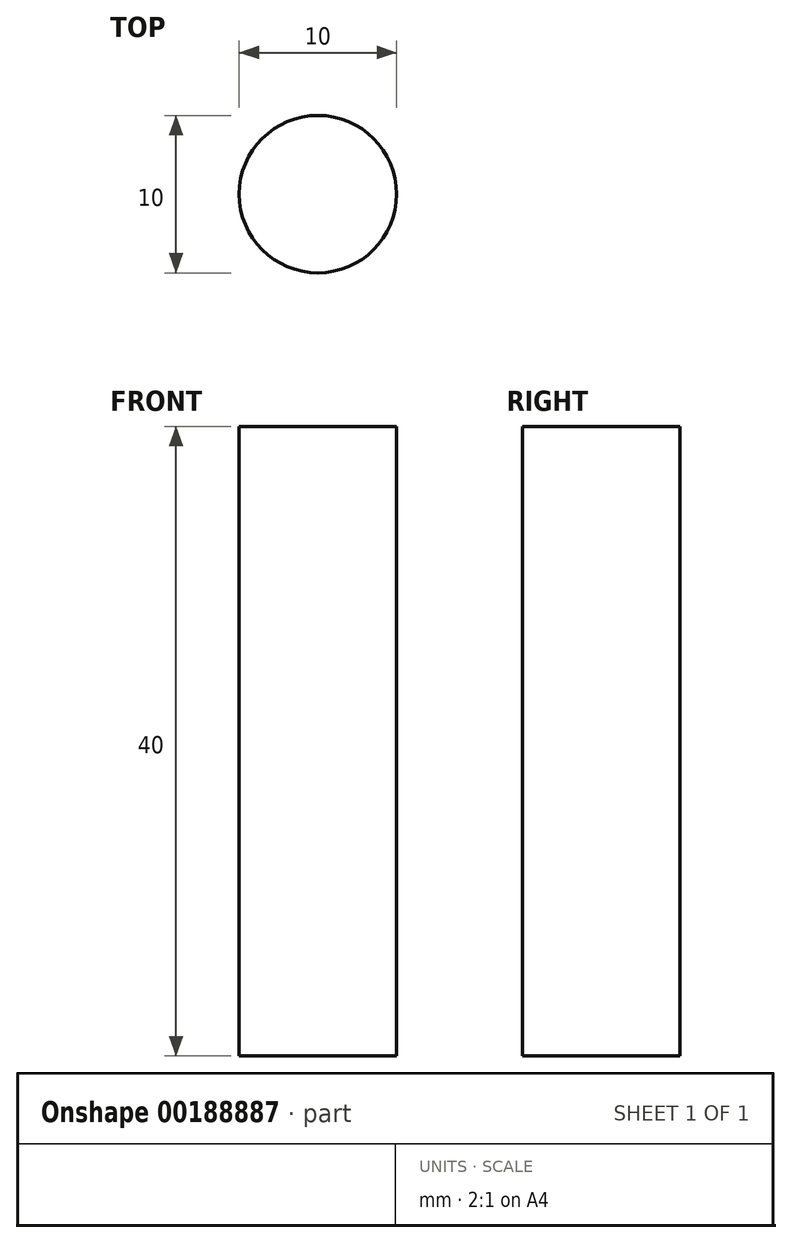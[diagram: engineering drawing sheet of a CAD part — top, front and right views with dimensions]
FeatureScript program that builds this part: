
annotation { "Feature Type Name" : "Feature", "Feature Type Description" : "" }
export const myFeature = defineFeature(function(context is Context, id is Id, definition is map)
    precondition{}
    {
        {
            var Q0;
            Q0=qCreatedBy(makeId("Top.planeOp"),FACE);
            var sketch = newSketch(context, id + "F0", { "sketchPlane" : qUnion([Q0])});
            skCircle(sketch, "E0", {"center": v(0, 0) * mm, "radius": 5 * mm});
            skSolve(sketch);
        }
        {
            var Q0;
            Q0 = qSketchRegion(id + "F0", true);
            extrude(context, id + "F1", {"entities" : qUnion([Q0]), "depth" : 40 * mm});
        }
    });
